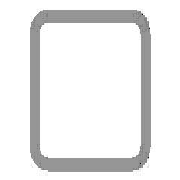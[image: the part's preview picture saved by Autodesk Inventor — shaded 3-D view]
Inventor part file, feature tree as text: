
AUTODESK INVENTOR PART (.ipt)
format: ipt  version: 2024 (Build 280153000, 153)  size: 129,024 bytes
history: native  units: mm (DEFAULTED — no unit token found)
features: other x4, extrude x1, sketch x1, plane x1
ambient origin geometry x8: Origin, YZ Plane, XZ Plane, XY Plane, X Axis, Y Axis, Z Axis, Center Point
bodies: Solid1 (feature_tree)
feature tree (7):
  parser-record x1  (decoder bookkeeping rows leaked as tree rows — omitted from the tree; the rows remain in map.json)
  other  "Driven Length"
  other  "Plano inicial"
  other  "Plano final"
  extrude  "Cuerpo"  TaperAngle=0.0deg  [1 undecoded]
  sketch  "Sketch3"  dims[d3=2200.0mm d4=0.0mm d10=50.8mm d11=50.8mm d12=3.175mm d13=-0.0mm d14=2200.0mm d15=25.4mm d16=25.4mm d17=6.35mm d18=90.0deg d19=2200.0mm]
  plane  "Work Plane3"
note: 1 required parameter value undecoded (feature->parameter linkage not recoverable at this tier; creation-order binding heuristic only, values carry confidence <= 0.55)
